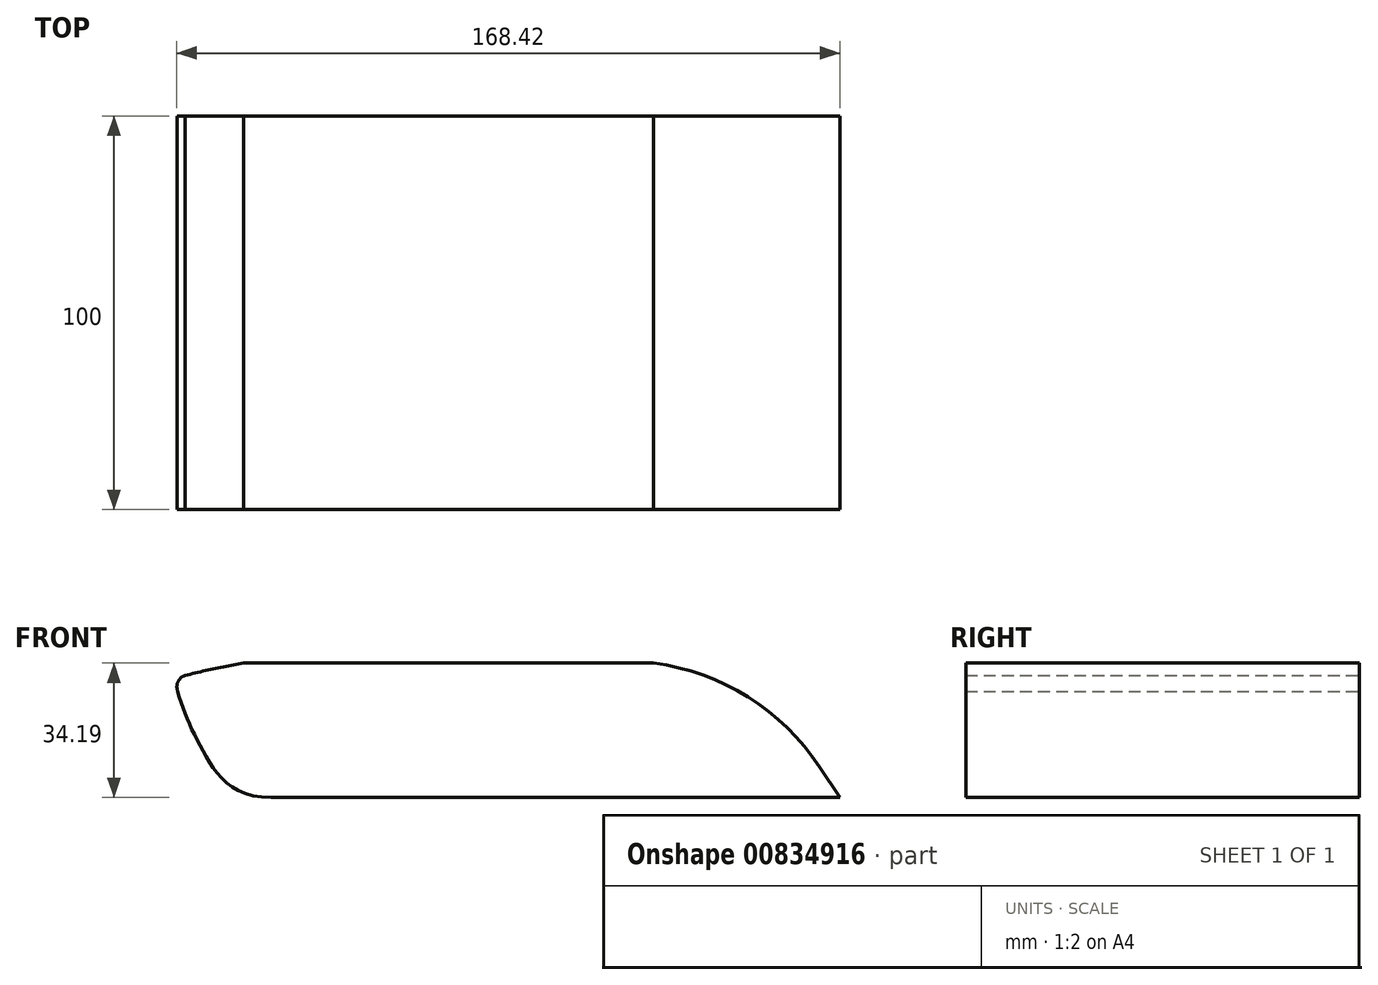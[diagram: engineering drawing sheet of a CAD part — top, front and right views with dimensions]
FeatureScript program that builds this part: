
annotation { "Feature Type Name" : "Feature", "Feature Type Description" : "" }
export const myFeature = defineFeature(function(context is Context, id is Id, definition is map)
    precondition{}
    {
        {
            var Q0;
            Q0=qCreatedBy(makeId("Front.planeOp"),FACE);
            var sketch = newSketch(context, id + "F0", { "sketchPlane" : qUnion([Q0])});
            skLineSegment(sketch, "E0.top", {"start": v(87.5, -20) * mm, "end": v(-87.5, -20) * mm, "construction": true});
            skLineSegment(sketch, "E0.left", {"start": v(87.5, 20) * mm, "end": v(87.5, -20) * mm, "construction": true});
            skLineSegment(sketch, "E0.right", {"start": v(-87.5, 20) * mm, "end": v(-87.5, -20) * mm, "construction": true});
            skPoint(sketch, "E0.middle", {"position": v(0, 0) * mm});
            skLineSegment(sketch, "E1", {"start": v(-87.5, 11.97) * mm, "end": v(87.5, 11.97) * mm, "construction": true});
            skLineSegment(sketch, "E2", {"start": v(-62.5, 11.97) * mm, "end": v(-62.5, -20) * mm, "construction": true});
            skLineSegment(sketch, "E3", {"start": v(-87.5, -14.6) * mm, "end": v(-62.5, -14.6) * mm, "construction": true});
            skPoint(sketch, "E4.endSnap0", {"position": v(-75, -14.6) * mm});
            skLineSegment(sketch, "E5", {"start": v(-71.67, -20) * mm, "end": v(-62.5, -20) * mm});
            skPoint(sketch, "E6.visualSharp", {"position": v(-75, -20) * mm});
            skLineSegment(sketch, "E7", {"start": v(-62.5, -20) * mm, "end": v(81.93, -20) * mm});
            skLineSegment(sketch, "E8", {"start": v(62.5, 11.97) * mm, "end": v(62.5, -20) * mm, "construction": true});
            skLineSegment(sketch, "E9", {"start": v(62.5, 11.97) * mm, "end": v(62.5, 20) * mm, "construction": true});
            skPoint(sketch, "E10.visualSharp", {"position": v(-87.5, 11.97) * mm});
            skArc(sketch, "E10.filletArc", {"start": v(-84.44, 11.02) * mm, "mid": v(-86.22, 9.42) * mm, "end": v(-86.26, 7.02) * mm});
            skPoint(sketch, "E11.visualSharp", {"position": v(62.5, 20) * mm});
            skLineSegment(sketch, "E12", {"start": v(-87.5, 16.97) * mm, "end": v(87.5, 16.97) * mm, "construction": true});
            skFitSpline(sketch, "E13", {"points": [v(87.5, -20) * mm, v(62.5, 11.97) * mm, v(49.8, 16.97) * mm, v(0, 16.97) * mm, v(-42.71, 16.97) * mm, v(-84.44, 11.02) * mm], "startDerivative": vector(-48.07, 199.6) * mm, "endDerivative": vector(-201.89, -51.46) * mm});
            skFitSpline(sketch, "E14", {"points": [v(-62.5, -20) * mm, v(-80.17, -7.6) * mm, v(-86.26, 7.02) * mm], "startDerivative": vector(-59.19, 0) * mm, "endDerivative": vector(-8.68, 33.69) * mm});
            skArc(sketch, "E15.filletArc", {"start": v(81.93, -20) * mm, "mid": v(85.28, -18.19) * mm, "end": v(85.6, -14.4) * mm});
            skSolve(sketch);
        }
        {
            var Q0;
            Q0 = qSketchRegion(id + "F0", true);
            extrude(context, id + "F1", {"entities" : qUnion([Q0]), "depth" : 100 * mm, "offsetDistance" : 25 * mm});
        }
        {
            var Q0;
            Q0=makeQuery(id+"F1.opExtrude","CAP_FACE",FACE,{"disambiguationData":[OSD([sQuery(id+"F0.wireOp",EDGE,"E7"),sQuery(id+"F0.wireOp",EDGE,"E10.filletArc"),sQuery(id+"F0.wireOp",EDGE,"E13"),sQuery(id+"F0.wireOp",EDGE,"E14"),sQuery(id+"F0.wireOp",EDGE,"E15.filletArc")])],"isStart":false});
            var sketch = newSketch(context, id + "F2", { "sketchPlane" : qUnion([Q0])});
            skLineSegment(sketch, "E16", {"start": v(81.93, -20) * mm, "end": v(76.78, -12.2) * mm});
            skPoint(sketch, "E17.visualSharp", {"position": v(59.1, 14.57) * mm});
            skArc(sketch, "E17.filletArc", {"start": v(76.78, -12.2) * mm, "mid": v(58.59, 5.56) * mm, "end": v(34.67, 14.2) * mm});
            skLineSegment(sketch, "E18", {"start": v(34.67, 14.2) * mm, "end": v(-69.53, 14.2) * mm});
            skLineSegment(sketch, "E19", {"start": v(-69.53, 14.2) * mm, "end": v(-74.97, 17.35) * mm});
            skLineSegment(sketch, "E20", {"start": v(-74.97, 17.35) * mm, "end": v(18.27, 25.82) * mm});
            skLineSegment(sketch, "E21", {"start": v(18.27, 25.82) * mm, "end": v(72.15, 22.62) * mm});
            skLineSegment(sketch, "E22", {"start": v(72.15, 22.62) * mm, "end": v(91.36, -5.64) * mm});
            skLineSegment(sketch, "E23", {"start": v(91.36, -5.64) * mm, "end": v(89.48, -23.34) * mm});
            skLineSegment(sketch, "E24", {"start": v(89.48, -23.34) * mm, "end": v(81.93, -20) * mm});
            skSolve(sketch);
        }
        {
            var Q0;
            Q0 = qSketchRegion(id + "F2", true);
            extrude(context, id + "F3", {"entities" : qUnion([Q0]), "operationType" : NewBodyOperationType.REMOVE, "endBound" : BoundingType.THROUGH_ALL, "oppositeDirection" : true, "depth" : 25 * mm, "offsetDistance" : 25 * mm});
        }
    });
